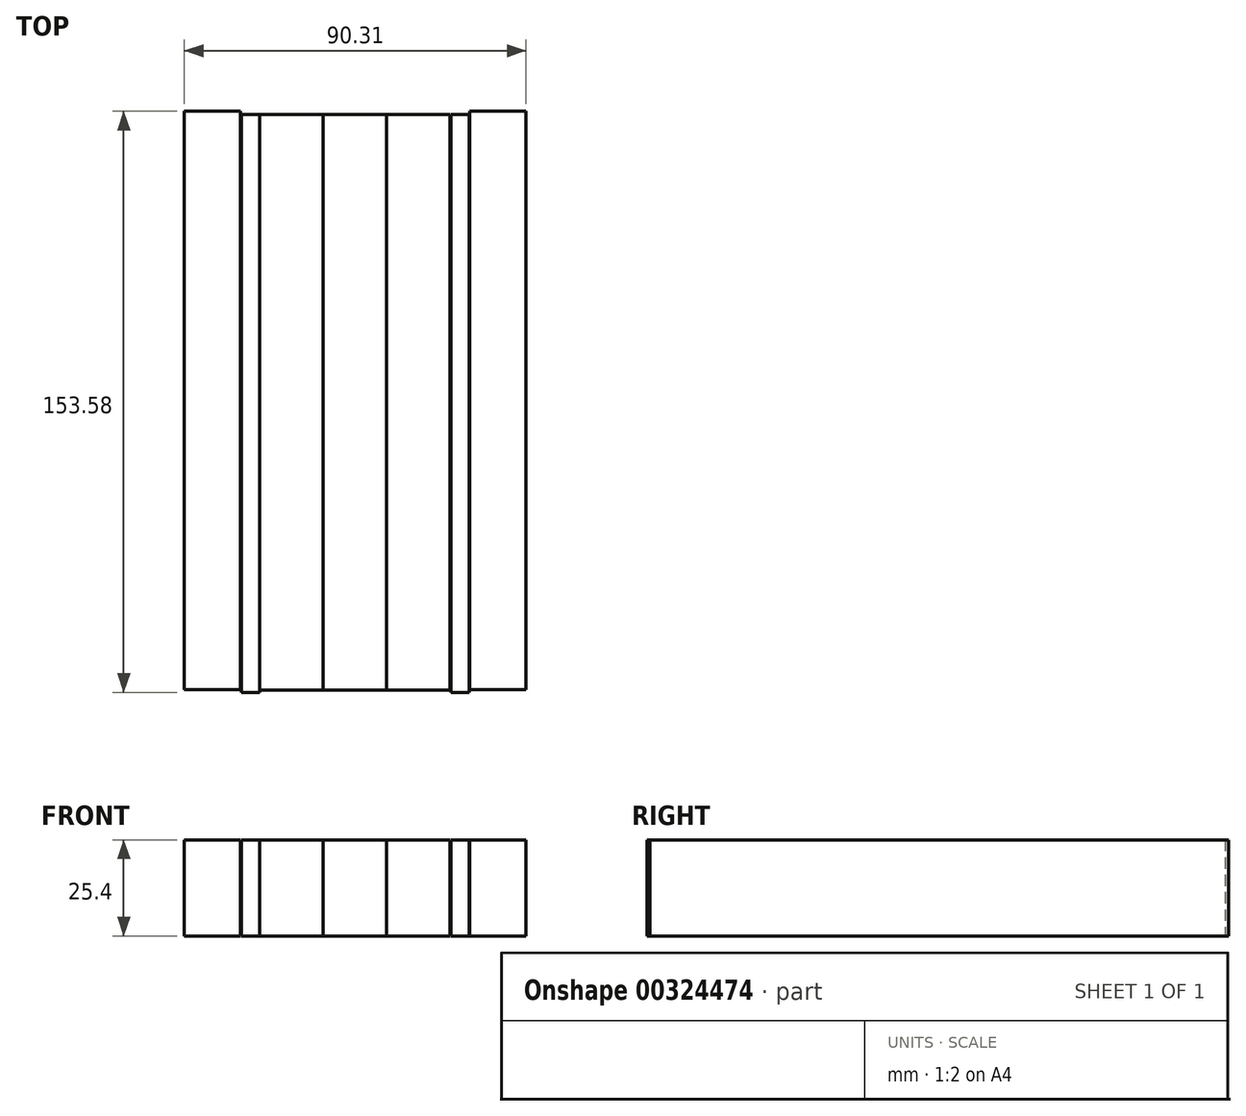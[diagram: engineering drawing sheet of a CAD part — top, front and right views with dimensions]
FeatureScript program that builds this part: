
annotation { "Feature Type Name" : "Feature", "Feature Type Description" : "" }
export const myFeature = defineFeature(function(context is Context, id is Id, definition is map)
    precondition{}
    {
        {
            var Q0;
            Q0=qCreatedBy(makeId("Top.planeOp"),FACE);
            var sketch = newSketch(context, id + "F0", { "sketchPlane" : qUnion([Q0])});
            skLineSegment(sketch, "E0.bottom", {"start": v(-75.83, 76.23) * mm, "end": v(-59.1, 76.23) * mm});
            skLineSegment(sketch, "E0.top", {"start": v(-75.83, -75.96) * mm, "end": v(-59.1, -75.96) * mm});
            skLineSegment(sketch, "E0.left", {"start": v(-75.83, 76.23) * mm, "end": v(-75.83, -75.96) * mm});
            skLineSegment(sketch, "E0.right", {"start": v(-59.1, 76.23) * mm, "end": v(-59.1, -75.96) * mm});
            skSolve(sketch);
        }
        {
            var Q0;
            Q0 = qSketchRegion(id + "F0", true);
            extrude(context, id + "F1", {"entities" : qUnion([Q0]), "depth" : 25.4 * mm});
        }
        {
            var Q0;
            Q0=makeQuery(id+"F1.opExtrude","SWEPT_BODY",BODY,{"disambiguationData":[OSD([sQuery(id+"F0.wireOp",EDGE,"E0.bottom"),sQuery(id+"F0.wireOp",EDGE,"E0.top"),sQuery(id+"F0.wireOp",EDGE,"E0.left"),sQuery(id+"F0.wireOp",EDGE,"E0.right")])]});
            transform(context, id + "F2", {"entities" : qUnion([Q0]), "transformType" : TransformType.TRANSLATION_3D, "dx" : 16.5 * mm, "dy" : 0 * mm, "dz" : 0 * mm, "makeCopy" : true});
        }
        {
            var Q0;
            Q0=makeQuery(id+"F2.opPattern","COPY",BODY,{"derivedFrom":makeQuery(id+"F1.opExtrude","SWEPT_BODY",BODY,{"disambiguationData":[OSD([sQuery(id+"F0.wireOp",EDGE,"E0.bottom"),sQuery(id+"F0.wireOp",EDGE,"E0.top"),sQuery(id+"F0.wireOp",EDGE,"E0.left"),sQuery(id+"F0.wireOp",EDGE,"E0.right")])]}),"instanceName":"1"});
            transform(context, id + "F3", {"entities" : qUnion([Q0]), "transformType" : TransformType.TRANSLATION_3D, "dx" : 16.5 * mm, "dy" : 0 * mm, "dz" : 0 * mm, "makeCopy" : true});
        }
        {
            var Q0;
            Q0=makeQuery(id+"F3.opPattern","COPY",BODY,{"derivedFrom":makeQuery(id+"F2.opPattern","COPY",BODY,{"derivedFrom":makeQuery(id+"F1.opExtrude","SWEPT_BODY",BODY,{"disambiguationData":[OSD([sQuery(id+"F0.wireOp",EDGE,"E0.bottom"),sQuery(id+"F0.wireOp",EDGE,"E0.top"),sQuery(id+"F0.wireOp",EDGE,"E0.left"),sQuery(id+"F0.wireOp",EDGE,"E0.right")])]}),"instanceName":"1"}),"instanceName":"1"});
            transform(context, id + "F4", {"entities" : qUnion([Q0]), "transformType" : TransformType.TRANSLATION_3D, "dx" : 16.76 * mm, "dy" : 0 * mm, "dz" : 0 * mm, "makeCopy" : true});
        }
        {
            var Q0;
            Q0=makeQuery(id+"F4.opPattern","COPY",BODY,{"derivedFrom":makeQuery(id+"F3.opPattern","COPY",BODY,{"derivedFrom":makeQuery(id+"F2.opPattern","COPY",BODY,{"derivedFrom":makeQuery(id+"F1.opExtrude","SWEPT_BODY",BODY,{"disambiguationData":[OSD([sQuery(id+"F0.wireOp",EDGE,"E0.bottom"),sQuery(id+"F0.wireOp",EDGE,"E0.top"),sQuery(id+"F0.wireOp",EDGE,"E0.left"),sQuery(id+"F0.wireOp",EDGE,"E0.right")])]}),"instanceName":"1"}),"instanceName":"1"}),"instanceName":"1"});
            transform(context, id + "F5", {"entities" : qUnion([Q0]), "transformType" : TransformType.TRANSLATION_3D, "dx" : 16.76 * mm, "dy" : 0 * mm, "dz" : 0 * mm, "makeCopy" : true});
        }
        {
            var Q0;
            Q0=makeQuery(id+"F5.opPattern","COPY",BODY,{"derivedFrom":makeQuery(id+"F4.opPattern","COPY",BODY,{"derivedFrom":makeQuery(id+"F3.opPattern","COPY",BODY,{"derivedFrom":makeQuery(id+"F2.opPattern","COPY",BODY,{"derivedFrom":makeQuery(id+"F1.opExtrude","SWEPT_BODY",BODY,{"disambiguationData":[OSD([sQuery(id+"F0.wireOp",EDGE,"E0.bottom"),sQuery(id+"F0.wireOp",EDGE,"E0.top"),sQuery(id+"F0.wireOp",EDGE,"E0.left"),sQuery(id+"F0.wireOp",EDGE,"E0.right")])]}),"instanceName":"1"}),"instanceName":"1"}),"instanceName":"1"}),"instanceName":"1"});
            transform(context, id + "F6", {"entities" : qUnion([Q0]), "transformType" : TransformType.TRANSLATION_3D, "dx" : 16.76 * mm, "dy" : 0 * mm, "dz" : 0 * mm, "makeCopy" : true});
        }
        {
            var Q0;
            Q0=makeQuery(id+"F6.opPattern","COPY",BODY,{"derivedFrom":makeQuery(id+"F5.opPattern","COPY",BODY,{"derivedFrom":makeQuery(id+"F4.opPattern","COPY",BODY,{"derivedFrom":makeQuery(id+"F3.opPattern","COPY",BODY,{"derivedFrom":makeQuery(id+"F2.opPattern","COPY",BODY,{"derivedFrom":makeQuery(id+"F1.opExtrude","SWEPT_BODY",BODY,{"disambiguationData":[OSD([sQuery(id+"F0.wireOp",EDGE,"E0.bottom"),sQuery(id+"F0.wireOp",EDGE,"E0.top"),sQuery(id+"F0.wireOp",EDGE,"E0.left"),sQuery(id+"F0.wireOp",EDGE,"E0.right")])]}),"instanceName":"1"}),"instanceName":"1"}),"instanceName":"1"}),"instanceName":"1"}),"instanceName":"1"});
            transform(context, id + "F7", {"entities" : qUnion([Q0]), "transformType" : TransformType.TRANSLATION_3D, "dx" : 17.02 * mm, "dy" : 0 * mm, "dz" : 0 * mm, "makeCopy" : true});
        }
        {
            var Q0;
            Q0=makeQuery(id+"F2.opPattern","COPY",BODY,{"derivedFrom":makeQuery(id+"F1.opExtrude","SWEPT_BODY",BODY,{"disambiguationData":[OSD([sQuery(id+"F0.wireOp",EDGE,"E0.bottom"),sQuery(id+"F0.wireOp",EDGE,"E0.top"),sQuery(id+"F0.wireOp",EDGE,"E0.left"),sQuery(id+"F0.wireOp",EDGE,"E0.right")])]}),"instanceName":"1"});
            deleteBodies(context, id + "F8", {"entities" : qUnion([Q0])});
        }
        {
            var Q0;
            Q0=qCreatedBy(makeId("Top.planeOp"),FACE);
            var sketch = newSketch(context, id + "F9", { "sketchPlane" : qUnion([Q0])});
            skLineSegment(sketch, "E1.bottom", {"start": v(-59.37, 76.23) * mm, "end": v(-54.5, 76.23) * mm});
            skLineSegment(sketch, "E1.top", {"start": v(-59.37, -76.5) * mm, "end": v(-54.5, -76.5) * mm});
            skLineSegment(sketch, "E1.left", {"start": v(-59.37, 76.23) * mm, "end": v(-59.37, -76.5) * mm});
            skLineSegment(sketch, "E1.right", {"start": v(-54.5, 76.23) * mm, "end": v(-54.5, -76.5) * mm});
            skSolve(sketch);
        }
        {
            var Q0;
            Q0=makeQuery(id+"F6.opPattern","COPY",BODY,{"derivedFrom":makeQuery(id+"F5.opPattern","COPY",BODY,{"derivedFrom":makeQuery(id+"F4.opPattern","COPY",BODY,{"derivedFrom":makeQuery(id+"F3.opPattern","COPY",BODY,{"derivedFrom":makeQuery(id+"F2.opPattern","COPY",BODY,{"derivedFrom":makeQuery(id+"F1.opExtrude","SWEPT_BODY",BODY,{"disambiguationData":[OSD([sQuery(id+"F0.wireOp",EDGE,"E0.bottom"),sQuery(id+"F0.wireOp",EDGE,"E0.top"),sQuery(id+"F0.wireOp",EDGE,"E0.left"),sQuery(id+"F0.wireOp",EDGE,"E0.right")])]}),"instanceName":"1"}),"instanceName":"1"}),"instanceName":"1"}),"instanceName":"1"}),"instanceName":"1"});
            deleteBodies(context, id + "F10", {"entities" : qUnion([Q0])});
        }
        {
            var Q0;
            Q0=makeQuery(id+"F9.imprint","IMPRINT",FACE,{"disambiguationData":[TD([[makeQuery(id+"F9.imprint","IMPRINT",EDGE,{"derivedFrom":sQuery(id+"F9.wireOp",EDGE,"E1.bottom")}),-1.0]])]});
            extrude(context, id + "F11", {"entities" : qUnion([Q0]), "depth" : 25.4 * mm});
        }
        {
            var Q0;
            Q0=makeQuery(id+"F11.opExtrude","SWEPT_BODY",BODY,{"disambiguationData":[OSD([sQuery(id+"F9.wireOp",EDGE,"E1.bottom"),sQuery(id+"F9.wireOp",EDGE,"E1.top"),sQuery(id+"F9.wireOp",EDGE,"E1.left"),sQuery(id+"F9.wireOp",EDGE,"E1.right")])]});
            transform(context, id + "F12", {"entities" : qUnion([Q0]), "transformType" : TransformType.TRANSLATION_3D, "dx" : 67.06 * mm, "dy" : 0 * mm, "dz" : 0 * mm, "makeCopy" : true});
        }
        {
            var Q0;
            Q0=makeQuery(id+"F11.opExtrude","SWEPT_BODY",BODY,{"disambiguationData":[OSD([sQuery(id+"F9.wireOp",EDGE,"E1.bottom"),sQuery(id+"F9.wireOp",EDGE,"E1.top"),sQuery(id+"F9.wireOp",EDGE,"E1.left"),sQuery(id+"F9.wireOp",EDGE,"E1.right")])]});
            deleteBodies(context, id + "F13", {"entities" : qUnion([Q0])});
        }
        {
            var Q0;
            Q0=makeQuery(id+"F12.opPattern","COPY",BODY,{"derivedFrom":makeQuery(id+"F11.opExtrude","SWEPT_BODY",BODY,{"disambiguationData":[OSD([sQuery(id+"F9.wireOp",EDGE,"E1.bottom"),sQuery(id+"F9.wireOp",EDGE,"E1.top"),sQuery(id+"F9.wireOp",EDGE,"E1.left"),sQuery(id+"F9.wireOp",EDGE,"E1.right")])]}),"instanceName":"1"});
            transform(context, id + "F14", {"entities" : qUnion([Q0]), "transformType" : TransformType.TRANSLATION_3D, "dx" : -55.37 * mm, "dy" : 0 * mm, "dz" : 0 * mm, "makeCopy" : true});
        }
        {
            var Q0;
            Q0=makeQuery(id+"F1.opExtrude","SWEPT_BODY",BODY,{"disambiguationData":[OSD([sQuery(id+"F0.wireOp",EDGE,"E0.bottom"),sQuery(id+"F0.wireOp",EDGE,"E0.top"),sQuery(id+"F0.wireOp",EDGE,"E0.left"),sQuery(id+"F0.wireOp",EDGE,"E0.right")])]});
            var Q1;
            Q1=makeQuery(id+"F7.opPattern","COPY",BODY,{"derivedFrom":makeQuery(id+"F6.opPattern","COPY",BODY,{"derivedFrom":makeQuery(id+"F5.opPattern","COPY",BODY,{"derivedFrom":makeQuery(id+"F4.opPattern","COPY",BODY,{"derivedFrom":makeQuery(id+"F3.opPattern","COPY",BODY,{"derivedFrom":makeQuery(id+"F2.opPattern","COPY",BODY,{"derivedFrom":makeQuery(id+"F1.opExtrude","SWEPT_BODY",BODY,{"disambiguationData":[OSD([sQuery(id+"F0.wireOp",EDGE,"E0.bottom"),sQuery(id+"F0.wireOp",EDGE,"E0.top"),sQuery(id+"F0.wireOp",EDGE,"E0.left"),sQuery(id+"F0.wireOp",EDGE,"E0.right")])]}),"instanceName":"1"}),"instanceName":"1"}),"instanceName":"1"}),"instanceName":"1"}),"instanceName":"1"}),"instanceName":"1"});
            deleteBodies(context, id + "F15", {"entities" : qUnion([Q0, Q1])});
        }
        {
            var Q0;
            Q0=qCreatedBy(makeId("Top.planeOp"),FACE);
            var sketch = newSketch(context, id + "F16", { "sketchPlane" : qUnion([Q0])});
            skLineSegment(sketch, "E2.bottom", {"start": v(-47.87, 77.08) * mm, "end": v(-62.74, 77.08) * mm});
            skLineSegment(sketch, "E2.top", {"start": v(-47.87, -75.72) * mm, "end": v(-62.74, -75.72) * mm});
            skLineSegment(sketch, "E2.left", {"start": v(-47.87, 77.08) * mm, "end": v(-47.87, -75.72) * mm});
            skLineSegment(sketch, "E2.right", {"start": v(-62.74, 77.08) * mm, "end": v(-62.74, -75.72) * mm});
            skSolve(sketch);
        }
        {
            var Q0;
            Q0=makeQuery(id+"F16.imprint","IMPRINT",FACE,{"disambiguationData":[TD([[makeQuery(id+"F16.imprint","IMPRINT",EDGE,{"derivedFrom":sQuery(id+"F16.wireOp",EDGE,"E2.bottom")}),1.0]])]});
            extrude(context, id + "F17", {"entities" : qUnion([Q0]), "depth" : 25.4 * mm});
        }
        {
            var Q0;
            Q0=makeQuery(id+"F17.opExtrude","SWEPT_BODY",BODY,{"disambiguationData":[OSD([sQuery(id+"F16.wireOp",EDGE,"E2.bottom"),sQuery(id+"F16.wireOp",EDGE,"E2.top"),sQuery(id+"F16.wireOp",EDGE,"E2.left"),sQuery(id+"F16.wireOp",EDGE,"E2.right")])]});
            transform(context, id + "F18", {"entities" : qUnion([Q0]), "transformType" : TransformType.TRANSLATION_3D, "dx" : 75.44 * mm, "dy" : 0 * mm, "dz" : 0 * mm, "makeCopy" : true});
        }
    });
